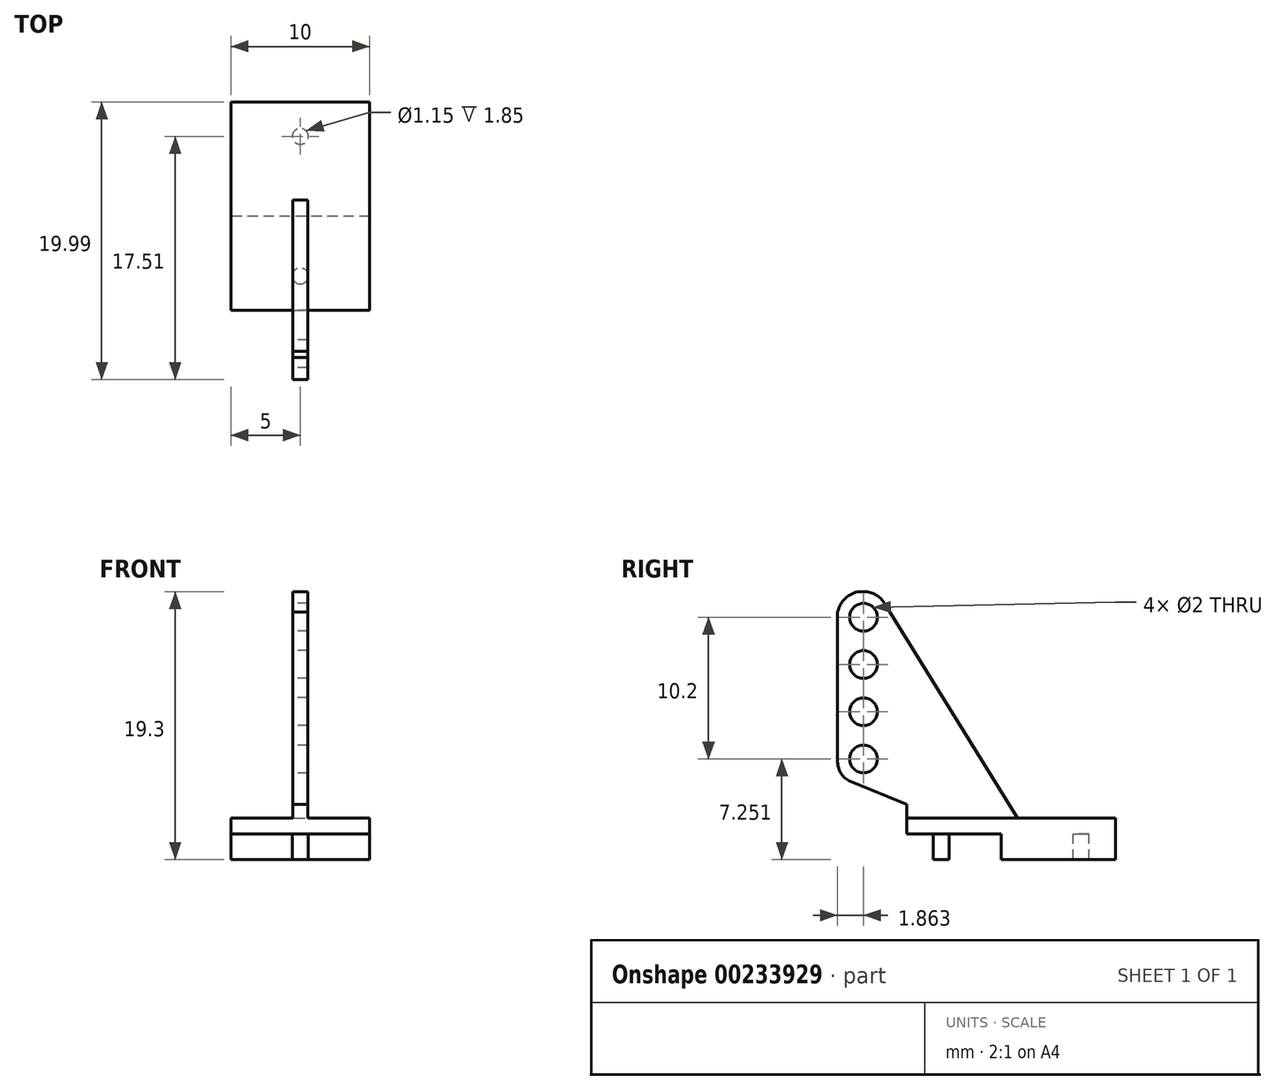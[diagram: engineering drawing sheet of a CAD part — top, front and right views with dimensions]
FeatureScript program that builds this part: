
annotation { "Feature Type Name" : "Feature", "Feature Type Description" : "" }
export const myFeature = defineFeature(function(context is Context, id is Id, definition is map)
    precondition{}
    {
        {
            var Q0;
            Q0=qCreatedBy(makeId("Top.planeOp"),FACE);
            var sketch = newSketch(context, id + "F0", { "sketchPlane" : qUnion([Q0])});
            skLineSegment(sketch, "E0.bottom", {"start": v(-5, 7.06) * mm, "end": v(5, 7.06) * mm});
            skLineSegment(sketch, "E0.top", {"start": v(-5, -7.94) * mm, "end": v(5, -7.94) * mm});
            skLineSegment(sketch, "E0.left", {"start": v(-5, 7.06) * mm, "end": v(-5, -7.94) * mm});
            skLineSegment(sketch, "E0.right", {"start": v(5, 7.06) * mm, "end": v(5, -7.94) * mm});
            skLineSegment(sketch, "E1", {"start": v(0, -7.94) * mm, "end": v(0, 0.06) * mm, "construction": true});
            skSolve(sketch);
        }
        {
            var Q0;
            Q0=makeQuery(id+"F0.imprint","IMPRINT",FACE,{"disambiguationData":[TD([[makeQuery(id+"F0.imprint","IMPRINT",EDGE,{"derivedFrom":sQuery(id+"F0.wireOp",EDGE,"E0.bottom")}),-1.0]])]});
            extrude(context, id + "F1", {"entities" : qUnion([Q0]), "depth" : 1.15 * mm});
        }
        {
            var Q0;
            Q0=makeQuery(id+"F1.opExtrude","CAP_FACE",FACE,{"disambiguationData":[OSD([sQuery(id+"F0.wireOp",EDGE,"E0.bottom"),sQuery(id+"F0.wireOp",EDGE,"E0.top"),sQuery(id+"F0.wireOp",EDGE,"E0.left"),sQuery(id+"F0.wireOp",EDGE,"E0.right")])],"isStart":true});
            var sketch = newSketch(context, id + "F2", { "sketchPlane" : qUnion([Q0])});
            skLineSegment(sketch, "E2", {"start": v(5, 0.44) * mm, "end": v(-5, 0.44) * mm, "construction": true});
            skCircle(sketch, "E3", {"center": v(5, 0.44) * mm, "radius": 0.72 * mm, "construction": true});
            skLineSegment(sketch, "E4", {"start": v(5, -0.28) * mm, "end": v(-5, -0.28) * mm});
            skLineSegment(sketch, "E5", {"start": v(5, 1.17) * mm, "end": v(-5, 1.17) * mm});
            skLineSegment(sketch, "E6", {"start": v(0, 1.17) * mm, "end": v(0, 5.47) * mm, "construction": true});
            skPoint(sketch, "E6.endSnap0", {"position": v(0, 1.17) * mm});
            skCircle(sketch, "E7", {"center": v(0, 5.47) * mm, "radius": 0.57 * mm});
            skCircle(sketch, "E8.MirrorC", {"center": v(0, -4.58) * mm, "radius": 0.57 * mm});
            skSolve(sketch);
        }
        {
            var Q0;
            {var subQ0=sQuery(id+"F2.wireOp",EDGE,"E4");Q0=makeQuery(id+"F2.imprint","IMPRINT",FACE,{"disambiguationData":[TD([[makeQuery(id+"F2.imprint","IMPRINT",EDGE,{"derivedFrom":subQ0}),-1.0]])]});}
            var Q1;
            Q1=makeQuery(id+"F2.imprint","IMPRINT",FACE,{"disambiguationData":[TD([[makeQuery(id+"F2.imprint","IMPRINT",EDGE,{"derivedFrom":sQuery(id+"F2.wireOp",EDGE,"E8.MirrorC")}),-1.0]])]});
            var Q2;
            Q2=makeQuery(id+"F2.imprint","IMPRINT",FACE,{"disambiguationData":[TD([[makeQuery(id+"F2.imprint","IMPRINT",EDGE,{"derivedFrom":sQuery(id+"F2.wireOp",EDGE,"E7")}),1.0]])]});
            extrude(context, id + "F3", {"entities" : qUnion([Q0, Q1, Q2]), "operationType" : NewBodyOperationType.ADD, "depth" : 1.85 * mm});
        }
        {
            var Q0;
            Q0=makeQuery(id+"F1.opExtrude","CAP_FACE",FACE,{"disambiguationData":[OSD([sQuery(id+"F0.wireOp",EDGE,"E0.bottom"),sQuery(id+"F0.wireOp",EDGE,"E0.top"),sQuery(id+"F0.wireOp",EDGE,"E0.left"),sQuery(id+"F0.wireOp",EDGE,"E0.right")])],"isStart":false});
            var sketch = newSketch(context, id + "F4", { "sketchPlane" : qUnion([Q0])});
            skLineSegment(sketch, "E9", {"start": v(0, -7.94) * mm, "end": v(0, 0.06) * mm, "construction": true});
            skPoint(sketch, "E9.endSnap0", {"position": v(0, -7.94) * mm});
            skSolve(sketch);
        }
        {
            var Q0;
            Q0=makeQuery(id+"F4.imprint","IMPRINT",FACE,{"disambiguationData":[TD([[makeQuery(id+"F4.imprint","IMPRINT",EDGE,{"derivedFrom":makeQuery(id+"F1.opExtrude","CAP_EDGE",EDGE,{"disambiguationData":[OSD([sQuery(id+"F0.wireOp",EDGE,"E0.bottom")])],"isStart":false})}),-1.0]])]});
            var sketch = newSketch(context, id + "F5", { "sketchPlane" : qUnion([Q0])});
            skLineSegment(sketch, "E10", {"start": v(0, -6.92) * mm, "end": v(0, -12.92) * mm, "construction": true});
            skCircle(sketch, "E11", {"center": v(0, -12.92) * mm, "radius": 0.55 * mm, "construction": true});
            skCircle(sketch, "E12", {"center": v(0, 0) * mm, "radius": 0.55 * mm, "construction": true});
            skLineSegment(sketch, "E13.bottom", {"start": v(-0.55, 0) * mm, "end": v(0.55, 0) * mm});
            skLineSegment(sketch, "E13.top", {"start": v(-0.55, -12.93) * mm, "end": v(0.55, -12.93) * mm});
            skLineSegment(sketch, "E13.left", {"start": v(-0.55, 0) * mm, "end": v(-0.55, -12.93) * mm});
            skLineSegment(sketch, "E13.right", {"start": v(0.55, 0) * mm, "end": v(0.55, -12.93) * mm});
            skSolve(sketch);
        }
        {
            var Q0;
            {var subQ0=sQuery(id+"F5.wireOp",EDGE,"E13.top");Q0=makeQuery(id+"F5.imprint","IMPRINT",FACE,{"disambiguationData":[TD([[makeQuery(id+"F5.imprint","IMPRINT",EDGE,{"derivedFrom":subQ0}),1.0]])]});}
            var Q1;
            {var subQ0=sQuery(id+"F5.wireOp",EDGE,"E13.bottom");Q1=makeQuery(id+"F5.imprint","IMPRINT",FACE,{"disambiguationData":[TD([[makeQuery(id+"F5.imprint","IMPRINT",EDGE,{"derivedFrom":subQ0}),-1.0]])]});}
            extrude(context, id + "F6", {"entities" : qUnion([Q0, Q1]), "operationType" : NewBodyOperationType.ADD, "depth" : 16.3 * mm});
        }
        {
            var Q0;
            Q0=makeQuery(id+"F6.opExtrude","SWEPT_FACE",FACE,{"disambiguationData":[OSD([sQuery(id+"F5.wireOp",EDGE,"E13.left")])]});
            var sketch = newSketch(context, id + "F7", { "sketchPlane" : qUnion([Q0])});
            skLineSegment(sketch, "E14", {"start": v(7.94, 1.15) * mm, "end": v(7.94, 2.14) * mm});
            skCircle(sketch, "E15", {"center": v(12.93, 1.15) * mm, "radius": 3 * mm, "construction": true});
            skLineSegment(sketch, "E16", {"start": v(7.94, 2.14) * mm, "end": v(11.99, 3.77) * mm});
            skLineSegment(sketch, "E17", {"start": v(12.93, 4.15) * mm, "end": v(12.93, 17.45) * mm});
            skPoint(sketch, "E18.first.point", {"position": v(12.93, 15.97) * mm});
            skPoint(sketch, "E18.second.point", {"position": v(11.34, 17.45) * mm});
            skPoint(sketch, "E18.third.point", {"position": v(9.31, 16.05) * mm});
            skLineSegment(sketch, "E19", {"start": v(12.93, 15.26) * mm, "end": v(12.93, 5.16) * mm});
            skPoint(sketch, "E20.visualSharp", {"position": v(12.93, 4.15) * mm});
            skArc(sketch, "E20.filletArc", {"start": v(11.99, 3.77) * mm, "mid": v(12.67, 4.32) * mm, "end": v(12.93, 5.16) * mm});
            skLineSegment(sketch, "E21", {"start": v(0, 1.15) * mm, "end": v(9.54, 16.59) * mm});
            skArc(sketch, "E22", {"start": v(12.93, 15.97) * mm, "mid": v(11.44, 17.43) * mm, "end": v(9.54, 16.59) * mm});
            skCircle(sketch, "E23", {"center": v(12.93, 1.15) * mm, "radius": 1.86 * mm, "construction": true});
            skLineSegment(sketch, "E24", {"start": v(11.07, 1.15) * mm, "end": v(11.07, 20.66) * mm, "construction": true});
            skCircle(sketch, "E25", {"center": v(11.07, 3.4) * mm, "radius": 2 * mm, "construction": true});
            skCircle(sketch, "E26", {"center": v(11.07, 5.4) * mm, "radius": 1 * mm});
            skCircle(sketch, "E27", {"center": v(11.07, 5.4) * mm, "radius": 3.4 * mm, "construction": true});
            skCircle(sketch, "E28", {"center": v(11.07, 8.8) * mm, "radius": 1 * mm});
            skCircle(sketch, "E29", {"center": v(11.07, 8.8) * mm, "radius": 3.4 * mm, "construction": true});
            skCircle(sketch, "E30", {"center": v(11.07, 12.2) * mm, "radius": 1 * mm});
            skCircle(sketch, "E31", {"center": v(11.07, 12.2) * mm, "radius": 3.4 * mm, "construction": true});
            skCircle(sketch, "E32", {"center": v(11.07, 15.6) * mm, "radius": 1 * mm});
            skSolve(sketch);
        }
        {
            var Q0;
            {var subQ0=sQuery(id+"F7.wireOp",EDGE,"E21");Q0=makeQuery(id+"F7.imprint","IMPRINT",FACE,{"disambiguationData":[TD([[makeQuery(id+"F7.imprint","IMPRINT",EDGE,{"derivedFrom":subQ0}),1.0]])]});}
            var Q1;
            {var subQ0=sQuery(id+"F7.wireOp",EDGE,"E17");var subQ1=makeQuery(id+"F6.opExtrude","CAP_EDGE",EDGE,{"disambiguationData":[OSD([sQuery(id+"F5.wireOp",EDGE,"E13.left")])],"isStart":false});var subQ2=makeQuery(id+"F7.imprint","INTERSECT",VERTEX,{"derivedFrom":[subQ1,subQ0]});Q1=makeQuery(id+"F7.imprint","IMPRINT",FACE,{"disambiguationData":[TD([[makeQuery(id+"F7.imprint","IMPRINT",EDGE,{"disambiguationData":[TD([[subQ2,-1.0]])],"derivedFrom":subQ0}),-1.0]])]});}
            var Q2;
            Q2=makeQuery(id+"F7.imprint","IMPRINT",FACE,{"disambiguationData":[TD([[makeQuery(id+"F7.imprint","IMPRINT",EDGE,{"derivedFrom":sQuery(id+"F7.wireOp",EDGE,"E32")}),1.0]])]});
            var Q3;
            Q3=makeQuery(id+"F7.imprint","IMPRINT",FACE,{"disambiguationData":[TD([[makeQuery(id+"F7.imprint","IMPRINT",EDGE,{"derivedFrom":sQuery(id+"F7.wireOp",EDGE,"E30")}),1.0]])]});
            var Q4;
            Q4=makeQuery(id+"F7.imprint","IMPRINT",FACE,{"disambiguationData":[TD([[makeQuery(id+"F7.imprint","IMPRINT",EDGE,{"derivedFrom":sQuery(id+"F7.wireOp",EDGE,"E28")}),1.0]])]});
            var Q5;
            Q5=makeQuery(id+"F7.imprint","IMPRINT",FACE,{"disambiguationData":[TD([[makeQuery(id+"F7.imprint","IMPRINT",EDGE,{"derivedFrom":sQuery(id+"F7.wireOp",EDGE,"E26")}),1.0]])]});
            var Q6;
            Q6=makeQuery(id+"F7.imprint","IMPRINT",FACE,{"disambiguationData":[TD([[makeQuery(id+"F7.imprint","IMPRINT",EDGE,{"derivedFrom":sQuery(id+"F7.wireOp",EDGE,"E14")}),-1.0]])]});
            extrude(context, id + "F8", {"entities" : qUnion([Q0, Q1, Q2, Q3, Q4, Q5, Q6]), "operationType" : NewBodyOperationType.REMOVE, "oppositeDirection" : true, "depth" : 3 * mm});
        }
    });
